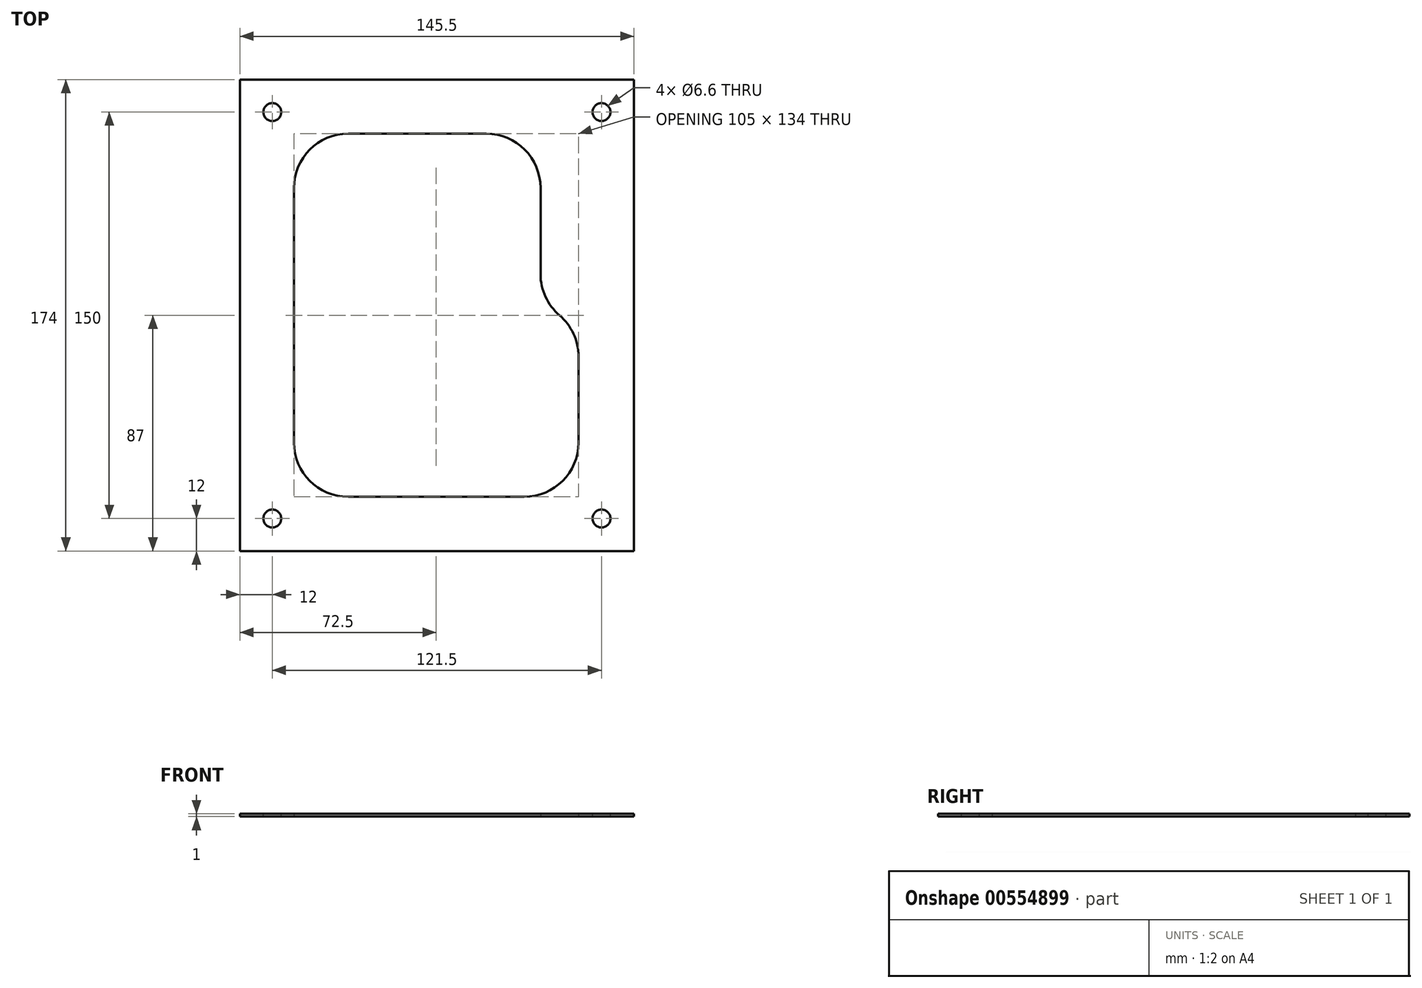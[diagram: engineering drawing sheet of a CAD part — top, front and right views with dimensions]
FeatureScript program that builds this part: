
annotation { "Feature Type Name" : "Feature", "Feature Type Description" : "" }
export const myFeature = defineFeature(function(context is Context, id is Id, definition is map)
    precondition{}
    {
        {
            var Q0;
            Q0=qCreatedBy(makeId("Top.planeOp"),FACE);
            var sketch = newSketch(context, id + "F0", { "sketchPlane" : qUnion([Q0])});
            skLineSegment(sketch, "E0", {"start": v(-52.75, 47) * mm, "end": v(-52.75, -47) * mm});
            skLineSegment(sketch, "E1", {"start": v(-32.75, 67) * mm, "end": v(18.25, 67) * mm});
            skLineSegment(sketch, "E2", {"start": v(38.25, 47) * mm, "end": v(38.25, 15.2) * mm});
            skLineSegment(sketch, "E3", {"start": v(32.25, -67) * mm, "end": v(-32.75, -67) * mm});
            skPoint(sketch, "E4.visualSharp", {"position": v(-52.75, 67) * mm});
            skArc(sketch, "E4.filletArc", {"start": v(-32.75, 67) * mm, "mid": v(-46.9, 61.14) * mm, "end": v(-52.75, 47) * mm});
            skPoint(sketch, "E5.visualSharp", {"position": v(-52.75, -67) * mm});
            skArc(sketch, "E5.filletArc", {"start": v(-52.75, -47) * mm, "mid": v(-46.9, -61.14) * mm, "end": v(-32.75, -67) * mm});
            skArc(sketch, "E6.filletArc", {"start": v(32.25, -67) * mm, "mid": v(46.4, -61.14) * mm, "end": v(52.25, -47) * mm});
            skPoint(sketch, "E7.visualSharp", {"position": v(38.25, 67) * mm});
            skArc(sketch, "E7.filletArc", {"start": v(38.25, 47) * mm, "mid": v(32.4, 61.14) * mm, "end": v(18.25, 67) * mm});
            skLineSegment(sketch, "E8", {"start": v(52.25, -15.2) * mm, "end": v(52.25, -47) * mm});
            skLineSegment(sketch, "E9", {"start": v(96.63, 0) * mm, "end": v(-154.13, 0) * mm, "construction": true});
            skArc(sketch, "E10", {"start": v(52.25, -15.2) * mm, "mid": v(50.42, -6.83) * mm, "end": v(45.25, 0) * mm});
            skArc(sketch, "E11", {"start": v(38.25, 15.2) * mm, "mid": v(40.08, 6.83) * mm, "end": v(45.25, 0) * mm});
            skLineSegment(sketch, "E12.bottom", {"start": v(72.75, 87) * mm, "end": v(-72.75, 87) * mm});
            skLineSegment(sketch, "E12.top", {"start": v(72.75, -87) * mm, "end": v(-72.75, -87) * mm});
            skLineSegment(sketch, "E12.left", {"start": v(72.75, 87) * mm, "end": v(72.75, -87) * mm});
            skLineSegment(sketch, "E12.right", {"start": v(-72.75, 87) * mm, "end": v(-72.75, -87) * mm});
            skPoint(sketch, "E12.middle", {"position": v(0, 0) * mm});
            skSolve(sketch);
        }
        {
            var Q0;
            Q0=makeQuery(id+"F0.imprint","IMPRINT",FACE,{"disambiguationData":[TD([[makeQuery(id+"F0.imprint","IMPRINT",EDGE,{"derivedFrom":sQuery(id+"F0.wireOp",EDGE,"E0")}),-1.0]])]});
            extrude(context, id + "F1", {"entities" : qUnion([Q0]), "depth" : 1 * mm, "offsetDistance" : 25.4 * mm});
        }
        {
            var Q0;
            Q0=makeQuery(id+"F1.opExtrude","CAP_FACE",FACE,{"disambiguationData":[OSD([sQuery(id+"F0.wireOp",EDGE,"E0"),sQuery(id+"F0.wireOp",EDGE,"E1"),sQuery(id+"F0.wireOp",EDGE,"E2"),sQuery(id+"F0.wireOp",EDGE,"E3"),sQuery(id+"F0.wireOp",EDGE,"E4.filletArc"),sQuery(id+"F0.wireOp",EDGE,"E5.filletArc"),sQuery(id+"F0.wireOp",EDGE,"E6.filletArc"),sQuery(id+"F0.wireOp",EDGE,"E7.filletArc"),sQuery(id+"F0.wireOp",EDGE,"E8"),sQuery(id+"F0.wireOp",EDGE,"E10"),sQuery(id+"F0.wireOp",EDGE,"E11"),sQuery(id+"F0.wireOp",EDGE,"E12.bottom"),sQuery(id+"F0.wireOp",EDGE,"E12.top"),sQuery(id+"F0.wireOp",EDGE,"E12.left"),sQuery(id+"F0.wireOp",EDGE,"E12.right")])],"isStart":false});
            var sketch = newSketch(context, id + "F2", { "sketchPlane" : qUnion([Q0])});
            skPoint(sketch, "E13", {"position": v(-60.75, 75) * mm});
            skPoint(sketch, "E14.MirrorP", {"position": v(60.75, 75) * mm});
            skPoint(sketch, "E15.MirrorP", {"position": v(-60.75, -75) * mm});
            skPoint(sketch, "E16.MirrorP", {"position": v(60.75, -75) * mm});
            skSolve(sketch);
        }
        {
            var Q0;
            Q0=sQuery(id+"F2.wireOp",VERTEX,"E13");
            var Q1;
            Q1=sQuery(id+"F2.wireOp",VERTEX,"E14.MirrorP");
            var Q2;
            Q2=sQuery(id+"F2.wireOp",VERTEX,"E16.MirrorP");
            var Q3;
            Q3=sQuery(id+"F2.wireOp",VERTEX,"E15.MirrorP");
            var Q4;
            Q4=makeQuery(id+"F1.opExtrude","SWEPT_BODY",BODY,{"disambiguationData":[OSD([sQuery(id+"F0.wireOp",EDGE,"E0"),sQuery(id+"F0.wireOp",EDGE,"E1"),sQuery(id+"F0.wireOp",EDGE,"E2"),sQuery(id+"F0.wireOp",EDGE,"E3"),sQuery(id+"F0.wireOp",EDGE,"E4.filletArc"),sQuery(id+"F0.wireOp",EDGE,"E5.filletArc"),sQuery(id+"F0.wireOp",EDGE,"E6.filletArc"),sQuery(id+"F0.wireOp",EDGE,"E7.filletArc"),sQuery(id+"F0.wireOp",EDGE,"E8"),sQuery(id+"F0.wireOp",EDGE,"E10"),sQuery(id+"F0.wireOp",EDGE,"E11"),sQuery(id+"F0.wireOp",EDGE,"E12.bottom"),sQuery(id+"F0.wireOp",EDGE,"E12.top"),sQuery(id+"F0.wireOp",EDGE,"E12.left"),sQuery(id+"F0.wireOp",EDGE,"E12.right")])]});
            hole(context, id + "F3", {"style" : HoleStyle.SIMPLE, "endStyle" : HoleEndStyle.THROUGH, "standardTappedOrClearance" : lookupTablePath({ "standard" : "ISO", "fit" : "Normal", "size" : "M6", "type" : "Clearance" }), "standardBlindInLast" : lookupTablePath({ "fit" : "Standard", "standard" : "ISO", "size" : "M6", "type" : "Clearance" }), "holeDiameter" : 6.6 * mm, "isTappedThrough" : true, "tappedDepth" : 12.7 * mm, "tapClearance" : 3, "locations" : qUnion([Q0, Q1, Q2, Q3]), "scope" : qUnion([Q4])});
        }
    });
